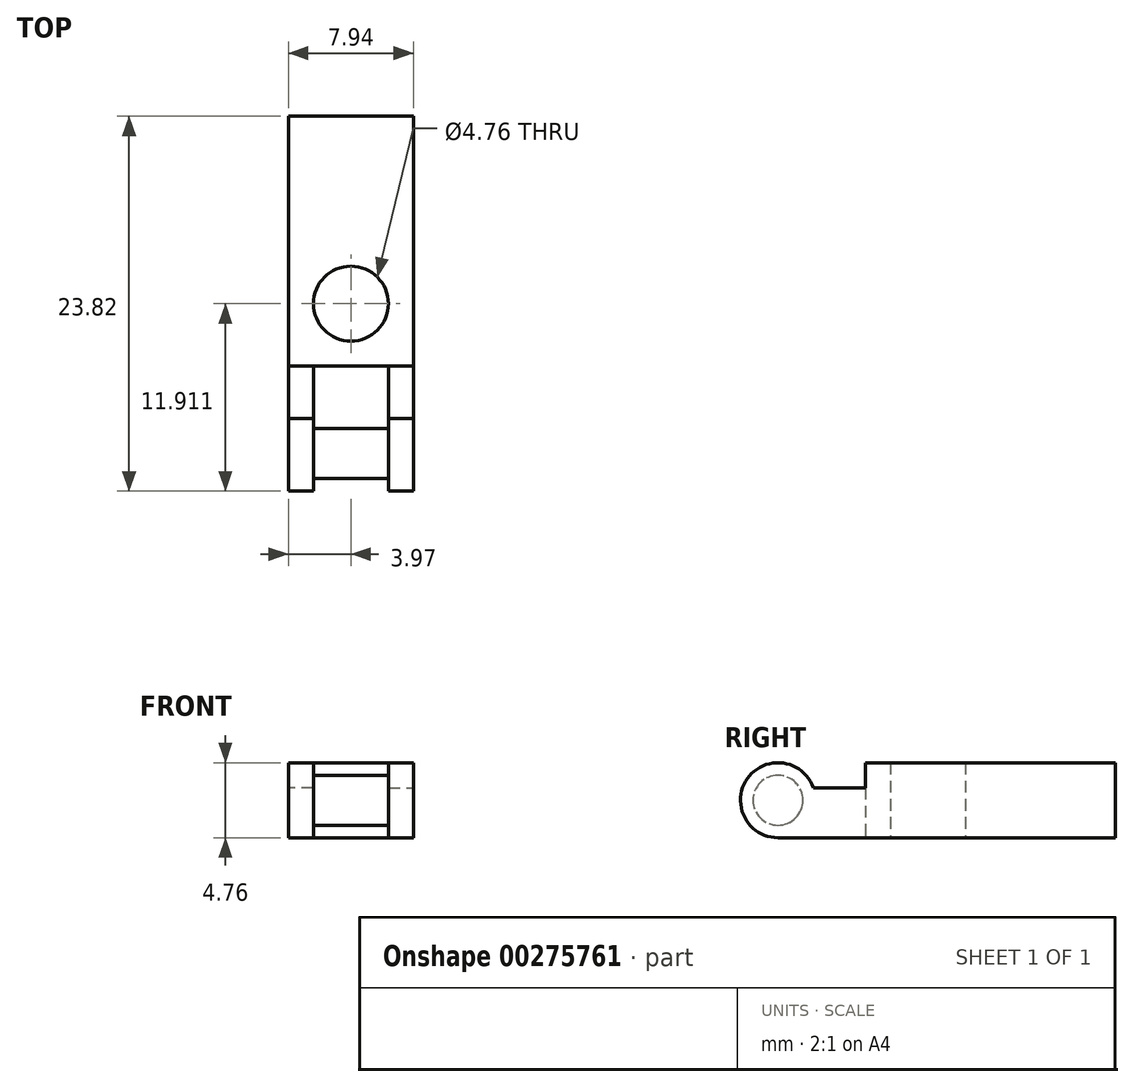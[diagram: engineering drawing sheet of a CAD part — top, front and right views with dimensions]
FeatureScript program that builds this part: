
annotation { "Feature Type Name" : "Feature", "Feature Type Description" : "" }
export const myFeature = defineFeature(function(context is Context, id is Id, definition is map)
    precondition{}
    {
        {
            var Q0;
            Q0=qCreatedBy(makeId("Top.planeOp"),FACE);
            var sketch = newSketch(context, id + "F0", { "sketchPlane" : qUnion([Q0])});
            skLineSegment(sketch, "E0.bottom", {"start": v(-3.97, 7.94) * mm, "end": v(3.97, 7.94) * mm});
            skLineSegment(sketch, "E0.top", {"start": v(-3.97, -7.94) * mm, "end": v(3.97, -7.94) * mm});
            skLineSegment(sketch, "E0.left", {"start": v(-3.97, 7.94) * mm, "end": v(-3.97, -7.94) * mm});
            skLineSegment(sketch, "E0.right", {"start": v(3.97, 7.94) * mm, "end": v(3.97, -7.94) * mm});
            skPoint(sketch, "E0.middle", {"position": v(0, 0) * mm});
            skCircle(sketch, "E1", {"center": v(0, 3.97) * mm, "radius": 2.38 * mm});
            skCircle(sketch, "E2.MirrorC", {"center": v(0, -3.97) * mm, "radius": 2.38 * mm});
            skSolve(sketch);
        }
        {
            var Q0;
            Q0=qSketchRegion(id+"F0",true);
            extrude(context, id + "F1", {"entities" : qUnion([Q0]), "depth" : 3.17 * mm});
        }
        {
            var Q0;
            Q0=makeQuery(id+"F0.imprint","IMPRINT",FACE,{"disambiguationData":[TD([[makeQuery(id+"F0.imprint","IMPRINT",EDGE,{"derivedFrom":sQuery(id+"F0.wireOp",EDGE,"E1")}),1.0]])]});
            var Q1;
            Q1=makeQuery(id+"F0.imprint","IMPRINT",FACE,{"disambiguationData":[TD([[makeQuery(id+"F0.imprint","IMPRINT",EDGE,{"derivedFrom":sQuery(id+"F0.wireOp",EDGE,"E2.MirrorC")}),-1.0]])]});
            extrude(context, id + "F2", {"entities" : qUnion([Q0, Q1]), "operationType" : NewBodyOperationType.ADD, "depth" : 4.76 * mm});
        }
        {
            var Q0;
            Q0=makeQuery(id+"F1.opExtrude","SWEPT_FACE",FACE,{"disambiguationData":[OSD([sQuery(id+"F0.wireOp",EDGE,"E0.left")])]});
            var sketch = newSketch(context, id + "F3", { "sketchPlane" : qUnion([Q0])});
            skLineSegment(sketch, "E3.bottom", {"start": v(7.94, 0) * mm, "end": v(11.11, 0) * mm});
            skLineSegment(sketch, "E3.top", {"start": v(7.94, 3.18) * mm, "end": v(11.11, 3.18) * mm});
            skLineSegment(sketch, "E3.left", {"start": v(7.94, 0) * mm, "end": v(7.94, 3.18) * mm});
            skLineSegment(sketch, "E3.right", {"start": v(11.11, 0) * mm, "end": v(11.11, 3.18) * mm});
            skLineSegment(sketch, "E4", {"start": v(13.5, 0) * mm, "end": v(13.5, 2.38) * mm});
            skCircle(sketch, "E5", {"center": v(13.5, 2.38) * mm, "radius": 2.38 * mm});
            skLineSegment(sketch, "E6", {"start": v(11.11, 3.18) * mm, "end": v(11.25, 3.18) * mm});
            skLineSegment(sketch, "E7", {"start": v(11.11, 0) * mm, "end": v(13.5, 0) * mm});
            skSolve(sketch);
        }
        {
            var Q0;
            Q0=qSketchRegion(id+"F3",true);
            extrude(context, id + "F4", {"entities" : qUnion([Q0]), "operationType" : NewBodyOperationType.ADD, "oppositeDirection" : true, "depth" : 1.59 * mm});
        }
        {
            var Q0;
            Q0=makeQuery(id+"F1.opExtrude","SWEPT_BODY",BODY,{"disambiguationData":[OSD([sQuery(id+"F0.wireOp",EDGE,"E0.bottom"),sQuery(id+"F0.wireOp",EDGE,"E0.top"),sQuery(id+"F0.wireOp",EDGE,"E0.left"),sQuery(id+"F0.wireOp",EDGE,"E0.right"),sQuery(id+"F0.wireOp",EDGE,"E1"),sQuery(id+"F0.wireOp",EDGE,"E2.MirrorC")])]});
            var Q1;
            Q1=qCreatedBy(makeId("Right.planeOp"),FACE);
            mirror(context, id + "F5", {"operationType" : NewBodyOperationType.ADD, "entities" : qUnion([Q0]), "mirrorPlane" : qUnion([Q1])});
        }
        {
            var Q0;
            Q0=makeQuery(id+"F4.opExtrude","CAP_FACE",FACE,{"disambiguationData":[OSD([sQuery(id+"F3.wireOp",EDGE,"E3.bottom"),sQuery(id+"F3.wireOp",EDGE,"E3.top"),sQuery(id+"F3.wireOp",EDGE,"E3.left"),sQuery(id+"F3.wireOp",EDGE,"E5"),sQuery(id+"F3.wireOp",EDGE,"E6"),sQuery(id+"F3.wireOp",EDGE,"E7")])],"isStart":false});
            var sketch = newSketch(context, id + "F6", { "sketchPlane" : qUnion([Q0])});
            skCircle(sketch, "E8", {"center": v(-13.5, 2.38) * mm, "radius": 1.59 * mm});
            skSolve(sketch);
        }
        {
            var Q0;
            Q0=qSketchRegion(id+"F6",true);
            extrude(context, id + "F7", {"entities" : qUnion([Q0]), "operationType" : NewBodyOperationType.ADD, "depth" : 4.76 * mm});
        }
    });
